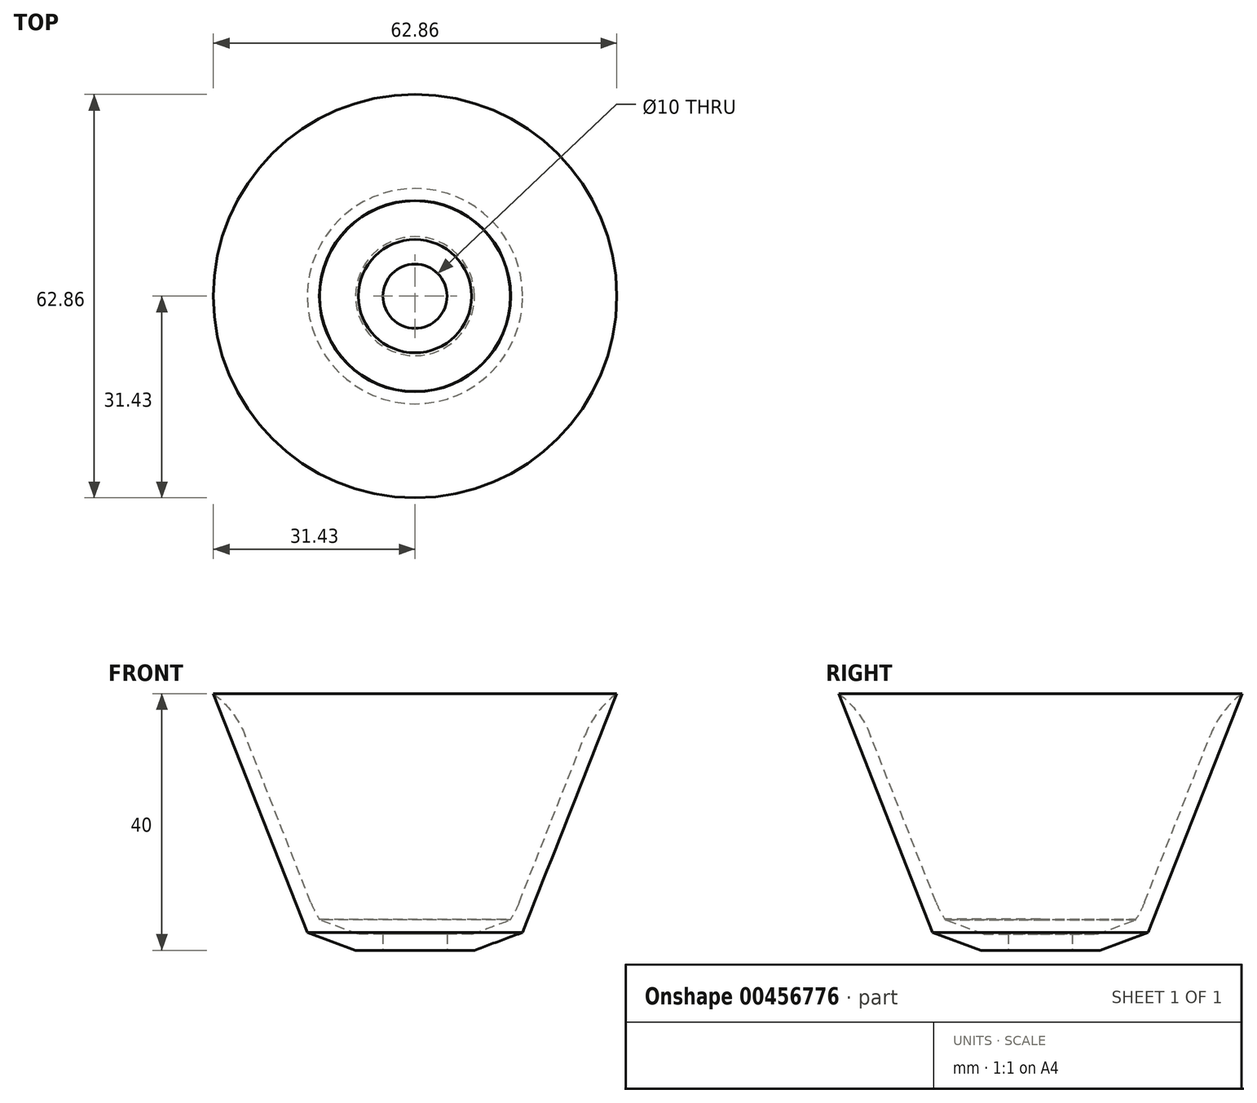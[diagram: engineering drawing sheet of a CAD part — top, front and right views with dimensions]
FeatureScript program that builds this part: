
annotation { "Feature Type Name" : "Feature", "Feature Type Description" : "" }
export const myFeature = defineFeature(function(context is Context, id is Id, definition is map)
    precondition{}
    {
        {
            var Q0;
            Q0=qCreatedBy(makeId("Front.planeOp"),FACE);
            var sketch = newSketch(context, id + "F0", { "sketchPlane" : qUnion([Q0])});
            skLineSegment(sketch, "E0", {"start": v(0, 0) * mm, "end": v(9.27, 0) * mm});
            skLineSegment(sketch, "E1", {"start": v(9.27, 0) * mm, "end": v(16.77, 2.78) * mm});
            skLineSegment(sketch, "E2", {"start": v(15.26, 5) * mm, "end": v(9.27, 2.78) * mm});
            skLineSegment(sketch, "E3", {"start": v(9.27, 2.78) * mm, "end": v(0, 2.78) * mm});
            skLineSegment(sketch, "E4", {"start": v(0, 2.78) * mm, "end": v(0, 0) * mm});
            skLineSegment(sketch, "E5", {"start": v(16.77, 2.78) * mm, "end": v(31.43, 40) * mm});
            skLineSegment(sketch, "E6", {"start": v(31.43, 40) * mm, "end": v(28.1, 37.57) * mm});
            skLineSegment(sketch, "E7", {"start": v(28.1, 37.57) * mm, "end": v(15.26, 5) * mm});
            skSolve(sketch);
        }
        {
            var Q0;
            Q0=makeQuery(id+"F0.imprint","IMPRINT",FACE,{"disambiguationData":[TD([[makeQuery(id+"F0.imprint","IMPRINT",EDGE,{"derivedFrom":sQuery(id+"F0.wireOp",EDGE,"E0")}),1.0]])]});
            var Q1;
            Q1=sQuery(id+"F0.wireOp",EDGE,"E4");
            revolve(context, id + "F1", {"entities" : qUnion([Q0]), "axis" : qUnion([Q1]), "revolveType" : RevolveType.FULL});
        }
        {
            var Q0;
            Q0=makeQuery(id+"F1.opRevolve","SWEPT_FACE",FACE,{"disambiguationData":[OSD([sQuery(id+"F0.wireOp",EDGE,"E3")])]});
            var Q1;
            Q1=makeQuery(id+"F1.opRevolve","SWEPT_FACE",FACE,{"disambiguationData":[OSD([sQuery(id+"F0.wireOp",EDGE,"E2")])]});
            var Q2;
            Q2=makeQuery(id+"F1.opRevolve","SWEPT_FACE",FACE,{"disambiguationData":[OSD([sQuery(id+"F0.wireOp",EDGE,"E6")])]});
            shell(context, id + "F2", {"entities" : qUnion([Q0, Q1, Q2]), "thickness" : 2.5 * mm});
        }
        {
            var Q0;
            Q0=makeQuery(id+"F1.opRevolve","SWEPT_FACE",FACE,{"disambiguationData":[OSD([sQuery(id+"F0.wireOp",EDGE,"E7")])]});
            fillet(context, id + "F3", {"entities" : qUnion([Q0]), "radius" : 15 * mm, "tangentPropagation" : true, "allowEdgeOverflow" : false});
        }
        {
            var Q0;
            Q0=makeQuery(id+"F1.opRevolve","SWEPT_FACE",FACE,{"disambiguationData":[OSD([sQuery(id+"F0.wireOp",EDGE,"E0")])]});
            var sketch = newSketch(context, id + "F4", { "sketchPlane" : qUnion([Q0])});
            skCircle(sketch, "E8", {"center": v(0, 0) * mm, "radius": 5 * mm});
            skSolve(sketch);
        }
        {
            var Q0;
            Q0=makeQuery(id+"F4.imprint","IMPRINT",FACE,{"disambiguationData":[TD([[makeQuery(id+"F4.imprint","IMPRINT",EDGE,{"derivedFrom":sQuery(id+"F4.wireOp",EDGE,"E8")}),1.0]])]});
            extrude(context, id + "F5", {"entities" : qUnion([Q0]), "operationType" : NewBodyOperationType.REMOVE, "endBound" : BoundingType.THROUGH_ALL, "oppositeDirection" : true, "depth" : 25 * mm});
        }
    });
